# Revit family: Faucet-Wall_Mount-Bath-KOHLER-Aleo_S-K-31238T_1
name_source: partatom
category: Plumbing Fixtures
units: mm (PartAtom-declared; Revit-internal decimal feet)

## family parameters
Cut with Voids When Loaded = No
Host = Face
Maintain Annotation Orientation = No
OmniClass Number = 23.31.11.00
Part Type = Normal
Room Calculation Point = No
Round Connector Dimension = Use Diameter
Shared = No

## types (3) — shared parameters
ADA Compliant = No
Assembly Code = D2010
CW Connection = Yes
Cold Water Inlet = Cold Water Inlet
Date Modified = 07/25/2022
Default Elevation = 36"
Description = Double Handle Wall Spout Bath Faucet (Ingenious)
Drain Included = No
Faucet Hole Spacing = 0"
Flow Rate = 13 GPM
HW Connection = Yes
Handle Clearance = 2 1/2"
Height = 2 5/16"
Hot Water Inlet = Hot Water Inlet
Length = 7 15/16"
Manufacturer = Kohler Co.
Master Format 2014 = 22 41 39
Master Format 2014 Name = Residential Faucets, Supplies, and Trim
Material = Premium Metal Construction
Pressure = 45.00 psi
Product Documentation Link = https://files.kohler.com.cn
Product Name = Aleo_S
Spout Reach = 7 15/16"
URL = http://www.kohler.com.cn
Vent Connection = No
Waste Connection = No
Waste Water Outlet = Waste Water Outlet
WaterSense Certified = No
Width = 7 7/8"

## per-type parameters (varying)
| type | Finish | Model | Product Page URL | Type |
| CP-Polished Chrome | Kohler-Metal-CP-Polished_Chrome | K-31238T-4-CP | https://www.kohler.com.cn | 1 |
| BL-Matte Black | Kohler-Metal-BL-Matte_Black | K-31238T-4-BL |  | 2 |
| 2BL-Black | KOHLER-Metal-2BL-Black | K-31238T-4-2BL | https://www.kohler.com.cn | 3 |

## geometry (parser evidence)
native form markers: Sweep x5
no freeform markers — native parametric forms only
